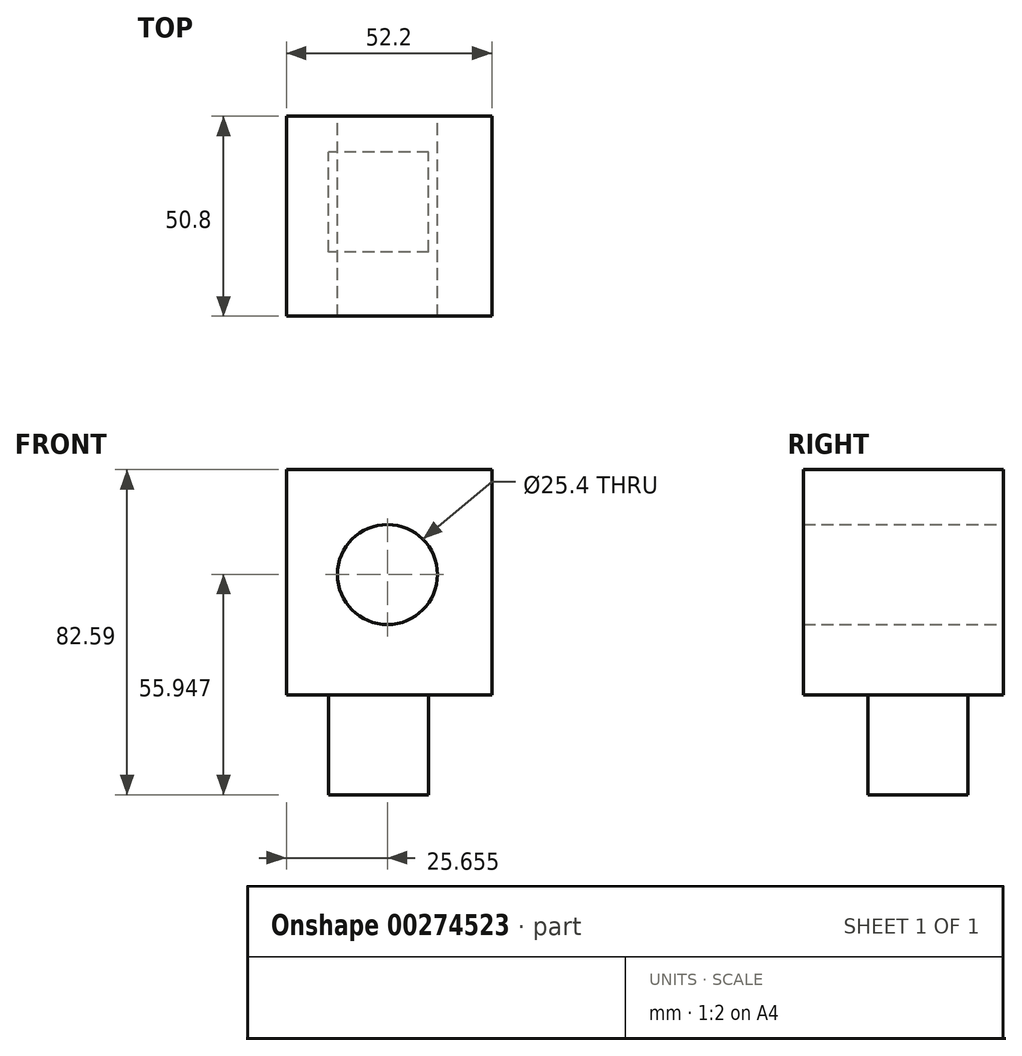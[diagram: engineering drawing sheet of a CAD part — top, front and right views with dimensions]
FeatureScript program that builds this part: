
annotation { "Feature Type Name" : "Feature", "Feature Type Description" : "" }
export const myFeature = defineFeature(function(context is Context, id is Id, definition is map)
    precondition{}
    {
        {
            var Q0;
            Q0=qCreatedBy(makeId("Front.planeOp"),FACE);
            var sketch = newSketch(context, id + "F0", { "sketchPlane" : qUnion([Q0])});
            skLineSegment(sketch, "E0.bottom", {"start": v(0, 0) * mm, "end": v(-52.2, 0) * mm});
            skLineSegment(sketch, "E0.top", {"start": v(0, 57.2) * mm, "end": v(-52.2, 57.2) * mm});
            skLineSegment(sketch, "E0.left", {"start": v(0, 0) * mm, "end": v(0, 57.2) * mm});
            skLineSegment(sketch, "E0.right", {"start": v(-52.2, 0) * mm, "end": v(-52.2, 57.2) * mm});
            skSolve(sketch);
        }
        {
            var Q0;
            Q0 = qSketchRegion(id + "F0", true);
            extrude(context, id + "F1", {"entities" : qUnion([Q0]), "depth" : 50.8 * mm});
        }
        {
            var Q0;
            Q0=makeQuery(id+"F1.opExtrude","CAP_FACE",FACE,{"disambiguationData":[OSD([sQuery(id+"F0.wireOp",EDGE,"E0.bottom"),sQuery(id+"F0.wireOp",EDGE,"E0.top"),sQuery(id+"F0.wireOp",EDGE,"E0.left"),sQuery(id+"F0.wireOp",EDGE,"E0.right")])],"isStart":true});
            var sketch = newSketch(context, id + "F2", { "sketchPlane" : qUnion([Q0])});
            skCircle(sketch, "E1", {"center": v(26.55, 30.55) * mm, "radius": 10.64 * mm});
            skSolve(sketch);
        }
        {
            var Q0;
            Q0=sQuery(id+"F2.wireOp",VERTEX,"E1.center");
            var Q1;
            Q1=makeQuery(id+"F1.opExtrude","SWEPT_BODY",BODY,{"disambiguationData":[OSD([sQuery(id+"F0.wireOp",EDGE,"E0.bottom"),sQuery(id+"F0.wireOp",EDGE,"E0.top"),sQuery(id+"F0.wireOp",EDGE,"E0.left"),sQuery(id+"F0.wireOp",EDGE,"E0.right")])]});
            hole(context, id + "F3", {"style" : HoleStyle.SIMPLE, "endStyle" : HoleEndStyle.THROUGH, "holeDiameter" : 25.4 * mm, "tappedDepth" : 12.7 * mm, "tapClearance" : 3, "locations" : qUnion([Q0]), "scope" : qUnion([Q1])});
        }
        {
            var Q0;
            Q0=makeQuery(id+"F1.opExtrude","SWEPT_FACE",FACE,{"disambiguationData":[OSD([sQuery(id+"F0.wireOp",EDGE,"E0.bottom")])]});
            var sketch = newSketch(context, id + "F4", { "sketchPlane" : qUnion([Q0])});
            skLineSegment(sketch, "E2.bottom", {"start": v(-16.07, 34.46) * mm, "end": v(-41.47, 34.46) * mm});
            skLineSegment(sketch, "E2.top", {"start": v(-16.07, 9.06) * mm, "end": v(-41.47, 9.06) * mm});
            skLineSegment(sketch, "E2.left", {"start": v(-16.07, 34.46) * mm, "end": v(-16.07, 9.06) * mm});
            skLineSegment(sketch, "E2.right", {"start": v(-41.47, 34.46) * mm, "end": v(-41.47, 9.06) * mm});
            skSolve(sketch);
        }
        {
            var Q0;
            Q0=makeQuery(id+"F4.imprint","IMPRINT",FACE,{"disambiguationData":[TD([[makeQuery(id+"F4.imprint","IMPRINT",EDGE,{"derivedFrom":sQuery(id+"F4.wireOp",EDGE,"E2.bottom")}),1.0]])]});
            extrude(context, id + "F5", {"entities" : qUnion([Q0]), "operationType" : NewBodyOperationType.ADD, "depth" : 25.4 * mm});
        }
    });
